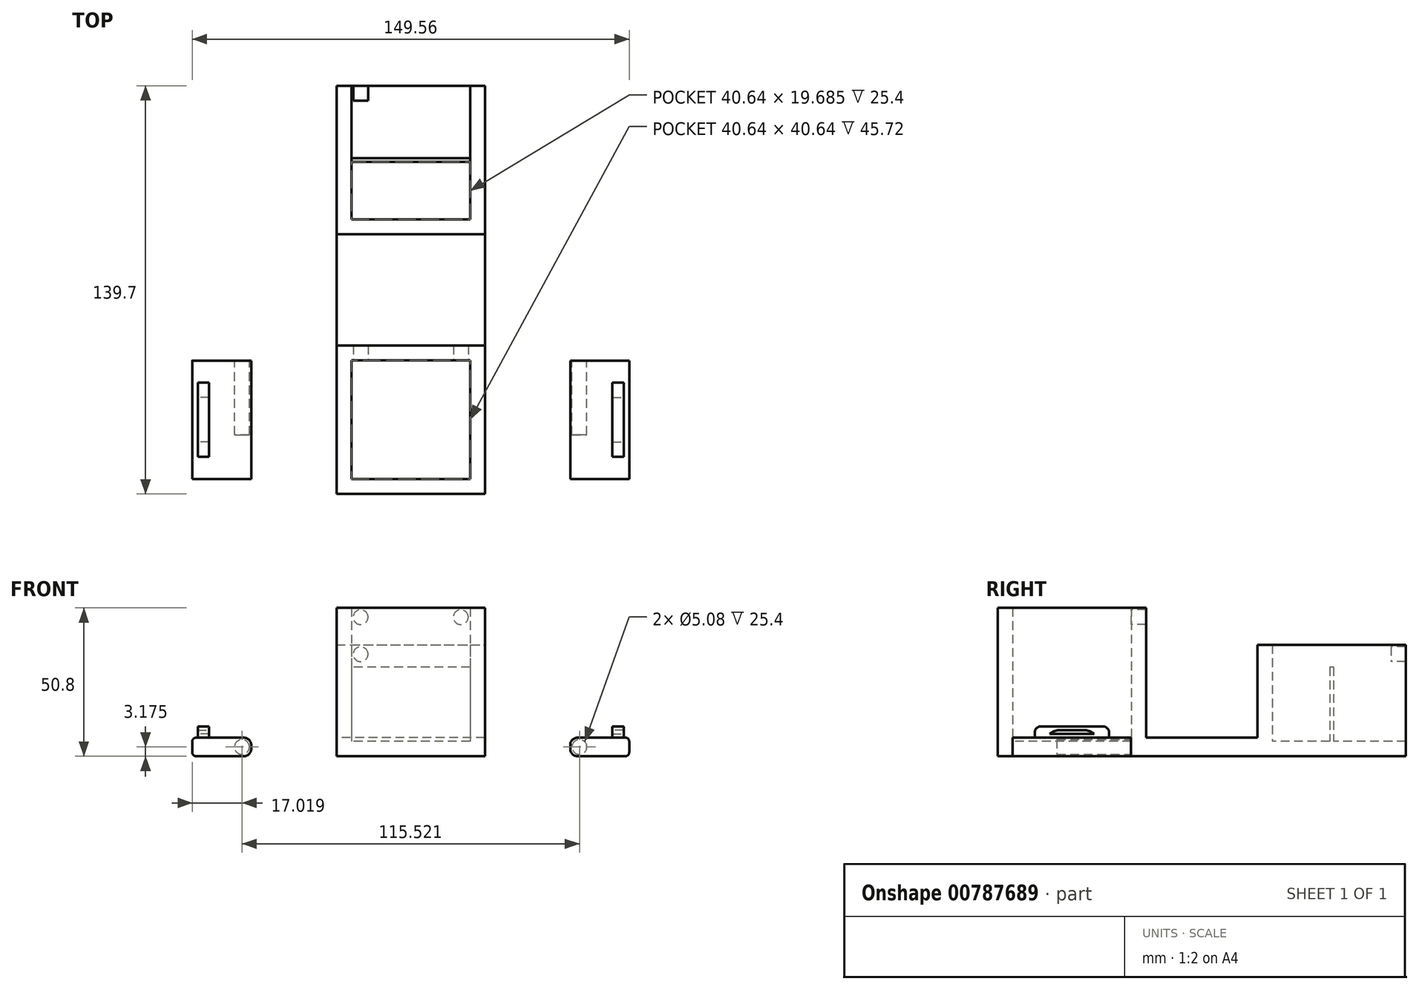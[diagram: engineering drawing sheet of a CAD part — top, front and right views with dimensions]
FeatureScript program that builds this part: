
annotation { "Feature Type Name" : "Feature", "Feature Type Description" : "" }
export const myFeature = defineFeature(function(context is Context, id is Id, definition is map)
    precondition{}
    {
        {
            var Q0;
            Q0=qCreatedBy(makeId("Top.planeOp"),FACE);
            var sketch = newSketch(context, id + "F0", { "sketchPlane" : qUnion([Q0])});
            skLineSegment(sketch, "E0.bottom", {"start": v(25.4, 25.4) * mm, "end": v(-25.4, 25.4) * mm});
            skLineSegment(sketch, "E0.top", {"start": v(25.4, -25.4) * mm, "end": v(-25.4, -25.4) * mm});
            skLineSegment(sketch, "E0.left", {"start": v(25.4, 25.4) * mm, "end": v(25.4, -25.4) * mm});
            skLineSegment(sketch, "E0.right", {"start": v(-25.4, 25.4) * mm, "end": v(-25.4, -25.4) * mm});
            skPoint(sketch, "E0.middle", {"position": v(0, 0) * mm});
            skLineSegment(sketch, "E1", {"start": v(-25.4, 25.4) * mm, "end": v(-25.4, 63.5) * mm});
            skLineSegment(sketch, "E2", {"start": v(25.4, 25.4) * mm, "end": v(25.4, 63.5) * mm});
            skLineSegment(sketch, "E3.bottom", {"start": v(-25.4, 63.5) * mm, "end": v(25.4, 63.5) * mm});
            skLineSegment(sketch, "E3.top", {"start": v(-25.4, 114.3) * mm, "end": v(25.4, 114.3) * mm});
            skLineSegment(sketch, "E3.left", {"start": v(-25.4, 63.5) * mm, "end": v(-25.4, 114.3) * mm});
            skLineSegment(sketch, "E3.right", {"start": v(25.4, 63.5) * mm, "end": v(25.4, 114.3) * mm});
            skSolve(sketch);
        }
        {
            var Q0;
            Q0=makeQuery(id+"F0.imprint","IMPRINT",FACE,{"disambiguationData":[TD([[makeQuery(id+"F0.imprint","IMPRINT",EDGE,{"derivedFrom":sQuery(id+"F0.wireOp",EDGE,"E0.bottom")}),1.0]])]});
            extrude(context, id + "F1", {"entities" : qUnion([Q0]), "depth" : 50.8 * mm, "offsetDistance" : 25.4 * mm});
        }
        {
            var Q0;
            Q0=makeQuery(id+"F0.imprint","IMPRINT",FACE,{"disambiguationData":[TD([[makeQuery(id+"F0.imprint","IMPRINT",EDGE,{"derivedFrom":sQuery(id+"F0.wireOp",EDGE,"E3.bottom")}),1.0]])]});
            extrude(context, id + "F2", {"entities" : qUnion([Q0]), "depth" : 38.1 * mm, "offsetDistance" : 25.4 * mm});
        }
        {
            var Q0;
            Q0=makeQuery(id+"F0.imprint","IMPRINT",FACE,{"disambiguationData":[TD([[makeQuery(id+"F0.imprint","IMPRINT",EDGE,{"derivedFrom":sQuery(id+"F0.wireOp",EDGE,"E0.bottom")}),-1.0]])]});
            extrude(context, id + "F3", {"entities" : qUnion([Q0]), "operationType" : NewBodyOperationType.ADD, "depth" : 6.35 * mm, "offsetDistance" : 25.4 * mm});
        }
        {
            var Q0;
            Q0=makeQuery(id+"F2.opExtrude","CAP_FACE",FACE,{"disambiguationData":[OSD([sQuery(id+"F0.wireOp",EDGE,"E3.bottom"),sQuery(id+"F0.wireOp",EDGE,"E3.top"),sQuery(id+"F0.wireOp",EDGE,"E3.left"),sQuery(id+"F0.wireOp",EDGE,"E3.right")])],"isStart":false});
            var Q1;
            Q1=makeQuery(id+"F1.opExtrude","CAP_FACE",FACE,{"disambiguationData":[OSD([sQuery(id+"F0.wireOp",EDGE,"E0.bottom"),sQuery(id+"F0.wireOp",EDGE,"E0.top"),sQuery(id+"F0.wireOp",EDGE,"E0.left"),sQuery(id+"F0.wireOp",EDGE,"E0.right")])],"isStart":false});
            shell(context, id + "F4", {"entities" : qUnion([Q0, Q1]), "thickness" : 5.08 * mm});
        }
        {
            var Q0;
            Q0=makeQuery(id+"F4.opShell","OFFSET_FACE",FACE,{"disambiguationData":[OSD([sQuery(id+"F0.wireOp",EDGE,"E0.top")])]});
            var sketch = newSketch(context, id + "F5", { "sketchPlane" : qUnion([Q0])});
            skLineSegment(sketch, "E4", {"start": v(-20.32, 50.8) * mm, "end": v(-17.15, 50.8) * mm});
            skLineSegment(sketch, "E5", {"start": v(20.32, 50.8) * mm, "end": v(17.14, 50.8) * mm});
            skLineSegment(sketch, "E6", {"start": v(17.14, 50.8) * mm, "end": v(17.14, 47.63) * mm});
            skLineSegment(sketch, "E7", {"start": v(-17.15, 50.8) * mm, "end": v(-17.15, 47.63) * mm});
            skCircle(sketch, "E8", {"center": v(-17.15, 47.63) * mm, "radius": 2.54 * mm});
            skCircle(sketch, "E9", {"center": v(17.14, 47.63) * mm, "radius": 2.54 * mm});
            skSolve(sketch);
        }
        {
            var Q0;
            Q0 = qSketchRegion(id + "F5", true);
            extrude(context, id + "F6", {"entities" : qUnion([Q0]), "operationType" : NewBodyOperationType.REMOVE, "depth" : 50.8 * mm, "offsetDistance" : 25.4 * mm});
        }
        {
            var Q0;
            Q0=qCreatedBy(makeId("Top.planeOp"),FACE);
            var sketch = newSketch(context, id + "F7", { "sketchPlane" : qUnion([Q0])});
            skLineSegment(sketch, "E10.bottom", {"start": v(-74.78, 20.26) * mm, "end": v(-54.59, 20.26) * mm});
            skLineSegment(sketch, "E10.top", {"start": v(-74.78, -20.26) * mm, "end": v(-54.59, -20.26) * mm});
            skLineSegment(sketch, "E10.left", {"start": v(-74.78, 20.26) * mm, "end": v(-74.78, -20.26) * mm});
            skLineSegment(sketch, "E10.right", {"start": v(-54.59, 20.26) * mm, "end": v(-54.59, -20.26) * mm});
            skPoint(sketch, "E10.middle", {"position": v(-64.68, 0) * mm});
            skSolve(sketch);
        }
        {
            var Q0;
            Q0 = qSketchRegion(id + "F7", true);
            extrude(context, id + "F8", {"entities" : qUnion([Q0]), "depth" : 6.35 * mm, "offsetDistance" : 25.4 * mm});
        }
        {
            var Q0;
            Q0=makeQuery(id+"F8.opExtrude","SWEPT_FACE",FACE,{"disambiguationData":[OSD([sQuery(id+"F7.wireOp",EDGE,"E10.bottom")])]});
            var sketch = newSketch(context, id + "F9", { "sketchPlane" : qUnion([Q0])});
            skLineSegment(sketch, "E11", {"start": v(54.59, 3.18) * mm, "end": v(57.76, 3.18) * mm});
            skCircle(sketch, "E12", {"center": v(57.76, 3.18) * mm, "radius": 2.54 * mm});
            skSolve(sketch);
        }
        {
            var Q0;
            Q0=makeQuery(id+"F8.opExtrude","CAP_FACE",FACE,{"disambiguationData":[OSD([sQuery(id+"F7.wireOp",EDGE,"E10.bottom"),sQuery(id+"F7.wireOp",EDGE,"E10.top"),sQuery(id+"F7.wireOp",EDGE,"E10.left"),sQuery(id+"F7.wireOp",EDGE,"E10.right")])],"isStart":false});
            var sketch = newSketch(context, id + "F10", { "sketchPlane" : qUnion([Q0])});
            skLineSegment(sketch, "E13", {"start": v(-74.78, 0) * mm, "end": v(-70.97, 0) * mm});
            skLineSegment(sketch, "E14.bottom", {"start": v(-72.9, 12.7) * mm, "end": v(-69.03, 12.7) * mm});
            skLineSegment(sketch, "E14.top", {"start": v(-72.9, -12.7) * mm, "end": v(-69.03, -12.7) * mm});
            skLineSegment(sketch, "E14.left", {"start": v(-72.9, 12.7) * mm, "end": v(-72.9, -12.7) * mm});
            skLineSegment(sketch, "E14.right", {"start": v(-69.03, 12.7) * mm, "end": v(-69.03, -12.7) * mm});
            skPoint(sketch, "E14.middle", {"position": v(-70.97, 0) * mm});
            skSolve(sketch);
        }
        {
            var Q0;
            {var subQ3=sQuery(id+"F10.wireOp",EDGE,"E14.bottom");Q0=makeQuery(id+"F10.imprint","IMPRINT",FACE,{"disambiguationData":[TD([[makeQuery(id+"F10.imprint","IMPRINT",EDGE,{"derivedFrom":subQ3}),-1.0]])]});}
            extrude(context, id + "F11", {"entities" : qUnion([Q0]), "operationType" : NewBodyOperationType.ADD, "depth" : 3.8 * mm, "offsetDistance" : 25.4 * mm});
        }
        {
            var Q0;
            Q0=makeQuery(id+"F11.opExtrude","SWEPT_FACE",FACE,{"disambiguationData":[OSD([sQuery(id+"F10.wireOp",EDGE,"E14.left")])]});
            var sketch = newSketch(context, id + "F12", { "sketchPlane" : qUnion([Q0])});
            skLineSegment(sketch, "E15", {"start": v(0, 6.35) * mm, "end": v(0, 10.16) * mm});
            skLineSegment(sketch, "E16.bottom", {"start": v(-7.62, 8.89) * mm, "end": v(7.62, 8.89) * mm});
            skLineSegment(sketch, "E16.top", {"start": v(-7.62, 7.62) * mm, "end": v(7.62, 7.62) * mm});
            skLineSegment(sketch, "E16.left", {"start": v(-7.62, 8.89) * mm, "end": v(-7.62, 7.62) * mm});
            skLineSegment(sketch, "E16.right", {"start": v(7.62, 8.89) * mm, "end": v(7.62, 7.62) * mm});
            skPoint(sketch, "E16.middle", {"position": v(0, 8.26) * mm});
            skSolve(sketch);
        }
        {
            var Q0;
            Q0 = qSketchRegion(id + "F12", true);
            extrude(context, id + "F13", {"entities" : qUnion([Q0]), "operationType" : NewBodyOperationType.REMOVE, "oppositeDirection" : true, "depth" : 25.4 * mm, "offsetDistance" : 25.4 * mm});
        }
        {
            var Q0;
            Q0=makeQuery(id+"F11.opExtrude","CAP_EDGE",EDGE,{"disambiguationData":[OSD([sQuery(id+"F10.wireOp",EDGE,"E14.top")])],"isStart":false});
            var Q1;
            Q1=makeQuery(id+"F11.opExtrude","CAP_EDGE",EDGE,{"disambiguationData":[OSD([sQuery(id+"F10.wireOp",EDGE,"E14.bottom")])],"isStart":false});
            var Q2;
            Q2=makeQuery(id+"F11.opExtrude","CAP_EDGE",EDGE,{"disambiguationData":[OSD([sQuery(id+"F10.wireOp",EDGE,"E14.bottom")])],"isStart":true});
            var Q3;
            Q3=makeQuery(id+"F11.opExtrude","CAP_EDGE",EDGE,{"disambiguationData":[OSD([sQuery(id+"F10.wireOp",EDGE,"E14.top")])],"isStart":true});
            fillet(context, id + "F14", {"entities" : qUnion([Q0, Q1, Q2, Q3]), "radius" : 1.9 * mm, "tangentPropagation" : true, "allowEdgeOverflow" : false});
        }
        {
            var Q0;
            Q0=makeQuery(id+"F13.boolean.opBoolean","COPY",EDGE,{"derivedFrom":makeQuery(id+"F13.opExtrude","SWEPT_EDGE",EDGE,{"disambiguationData":[OSD([sQuery(id+"F12.wireOp",EDGE,"E16.bottom"),sQuery(id+"F12.wireOp",EDGE,"E16.right")])]})});
            var Q1;
            Q1=makeQuery(id+"F13.boolean.opBoolean","COPY",EDGE,{"derivedFrom":makeQuery(id+"F13.opExtrude","SWEPT_EDGE",EDGE,{"disambiguationData":[OSD([sQuery(id+"F12.wireOp",EDGE,"E16.bottom"),sQuery(id+"F12.wireOp",EDGE,"E16.left")])]})});
            fillet(context, id + "F15", {"entities" : qUnion([Q0, Q1]), "radius" : 5.08 * mm, "tangentPropagation" : true, "allowEdgeOverflow" : false});
        }
        {
            var Q0;
            Q0=makeQuery(id+"F4.opShell","OFFSET_FACE",FACE,{"disambiguationData":[OSD([sQuery(id+"F0.wireOp",EDGE,"E3.bottom")])]});
            var sketch = newSketch(context, id + "F16", { "sketchPlane" : qUnion([Q0])});
            skLineSegment(sketch, "E17", {"start": v(-20.32, 38.1) * mm, "end": v(-17.15, 38.1) * mm});
            skLineSegment(sketch, "E18", {"start": v(-17.15, 38.1) * mm, "end": v(-17.15, 34.93) * mm});
            skCircle(sketch, "E19", {"center": v(-17.15, 34.93) * mm, "radius": 2.54 * mm});
            skCircle(sketch, "E20.MirrorC", {"center": v(17.15, 34.93) * mm, "radius": 2.54 * mm});
            skSolve(sketch);
        }
        {
            var Q0;
            Q0=makeQuery(id+"F16.imprint","IMPRINT",FACE,{"disambiguationData":[TD([[makeQuery(id+"F16.imprint","IMPRINT",EDGE,{"derivedFrom":sQuery(id+"F16.wireOp",EDGE,"E19")}),1.0]])]});
            var Q1;
            Q1=makeQuery(id+"F16.imprint","IMPRINT",FACE,{"disambiguationData":[TD([[makeQuery(id+"F16.imprint","IMPRINT",EDGE,{"derivedFrom":sQuery(id+"F16.wireOp",EDGE,"E20.MirrorC")}),-1.0]])]});
            extrude(context, id + "F17", {"entities" : qUnion([Q0, Q1]), "operationType" : NewBodyOperationType.REMOVE, "depth" : 50.8 * mm, "offsetDistance" : 25.4 * mm});
        }
        {
            var Q0;
            Q0=makeQuery(id+"F8.opExtrude","CAP_EDGE",EDGE,{"disambiguationData":[OSD([sQuery(id+"F7.wireOp",EDGE,"E10.right")])],"isStart":false});
            var Q1;
            Q1=makeQuery(id+"F8.opExtrude","CAP_EDGE",EDGE,{"disambiguationData":[OSD([sQuery(id+"F7.wireOp",EDGE,"E10.right")])],"isStart":true});
            var Q2;
            Q2=makeQuery(id+"FwgZroeMugeXsrW_2.opPattern","COPY",EDGE,{"derivedFrom":makeQuery(id+"F8.opExtrude","CAP_EDGE",EDGE,{"disambiguationData":[OSD([sQuery(id+"F7.wireOp",EDGE,"E10.right")])],"isStart":false}),"instanceName":"1"});
            var Q3;
            Q3=makeQuery(id+"FwgZroeMugeXsrW_2.opPattern","COPY",EDGE,{"derivedFrom":makeQuery(id+"F8.opExtrude","CAP_EDGE",EDGE,{"disambiguationData":[OSD([sQuery(id+"F7.wireOp",EDGE,"E10.right")])],"isStart":true}),"instanceName":"1"});
            fillet(context, id + "F18", {"entities" : qUnion([Q0, Q1, Q2, Q3]), "radius" : 2.54 * mm, "tangentPropagation" : true, "allowEdgeOverflow" : false});
        }
        {
            var Q0;
            Q0=makeQuery(id+"FwgZroeMugeXsrW_2.opPattern","COPY",EDGE,{"derivedFrom":makeQuery(id+"F8.opExtrude","CAP_EDGE",EDGE,{"disambiguationData":[OSD([sQuery(id+"F7.wireOp",EDGE,"E10.left")])],"isStart":false}),"instanceName":"1"});
            var Q1;
            Q1=makeQuery(id+"FwgZroeMugeXsrW_2.opPattern","COPY",EDGE,{"derivedFrom":makeQuery(id+"F8.opExtrude","CAP_EDGE",EDGE,{"disambiguationData":[OSD([sQuery(id+"F7.wireOp",EDGE,"E10.left")])],"isStart":true}),"instanceName":"1"});
            var Q2;
            Q2=makeQuery(id+"F8.opExtrude","CAP_EDGE",EDGE,{"disambiguationData":[OSD([sQuery(id+"F7.wireOp",EDGE,"E10.left")])],"isStart":false});
            var Q3;
            Q3=makeQuery(id+"F8.opExtrude","CAP_EDGE",EDGE,{"disambiguationData":[OSD([sQuery(id+"F7.wireOp",EDGE,"E10.left")])],"isStart":true});
            fillet(context, id + "F19", {"entities" : qUnion([Q0, Q1, Q2, Q3]), "radius" : 1.27 * mm, "tangentPropagation" : true, "allowEdgeOverflow" : false});
        }
        {
            var Q0;
            Q0=makeQuery(id+"F4.opShell","OFFSET_FACE",FACE,{"disambiguationData":[OSD([sQuery(id+"F0.wireOp",EDGE,"E0.bottom"),sQuery(id+"F0.wireOp",EDGE,"E0.top"),sQuery(id+"F0.wireOp",EDGE,"E0.left"),sQuery(id+"F0.wireOp",EDGE,"E0.right"),sQuery(id+"F0.wireOp",EDGE,"E1"),sQuery(id+"F0.wireOp",EDGE,"E2"),sQuery(id+"F0.wireOp",EDGE,"E3.bottom"),sQuery(id+"F0.wireOp",EDGE,"E3.top"),sQuery(id+"F0.wireOp",EDGE,"E3.left"),sQuery(id+"F0.wireOp",EDGE,"E3.right")]),OD(1.0)]});
            var sketch = newSketch(context, id + "F20", { "sketchPlane" : qUnion([Q0])});
            skLineSegment(sketch, "E21", {"start": v(-20.32, 88.9) * mm, "end": v(20.32, 88.9) * mm});
            skLineSegment(sketch, "E22.bottom", {"start": v(20.32, 89.53) * mm, "end": v(-20.32, 89.53) * mm});
            skLineSegment(sketch, "E22.top", {"start": v(20.32, 88.27) * mm, "end": v(-20.32, 88.27) * mm});
            skLineSegment(sketch, "E22.left", {"start": v(20.32, 89.54) * mm, "end": v(20.32, 88.27) * mm});
            skLineSegment(sketch, "E22.right", {"start": v(-20.32, 89.53) * mm, "end": v(-20.32, 88.27) * mm});
            skPoint(sketch, "E22.middle", {"position": v(0, 88.9) * mm});
            skSolve(sketch);
        }
        {
            var Q0;
            Q0 = qSketchRegion(id + "F20", true);
            extrude(context, id + "F21", {"entities" : qUnion([Q0]), "operationType" : NewBodyOperationType.ADD, "depth" : 25.4 * mm, "offsetDistance" : 25.4 * mm});
        }
        {
            var Q0;
            Q0=makeQuery(id+"F9.imprint","IMPRINT",FACE,{"disambiguationData":[TD([[makeQuery(id+"F9.imprint","IMPRINT",EDGE,{"derivedFrom":sQuery(id+"F9.wireOp",EDGE,"E12")}),1.0]])]});
            extrude(context, id + "F22", {"entities" : qUnion([Q0]), "operationType" : NewBodyOperationType.REMOVE, "oppositeDirection" : true, "depth" : 25.4 * mm, "offsetDistance" : 25.4 * mm});
        }
        {
            var Q0;
            Q0=makeQuery(id+"F8.opExtrude","SWEPT_BODY",BODY,{"disambiguationData":[OSD([sQuery(id+"F7.wireOp",EDGE,"E10.bottom"),sQuery(id+"F7.wireOp",EDGE,"E10.top"),sQuery(id+"F7.wireOp",EDGE,"E10.left"),sQuery(id+"F7.wireOp",EDGE,"E10.right")])]});
            var Q1;
            Q1=qCreatedBy(makeId("Right.planeOp"),FACE);
            mirror(context, id + "F23", {"entities" : qUnion([Q0]), "mirrorPlane" : qUnion([Q1])});
        }
    });
